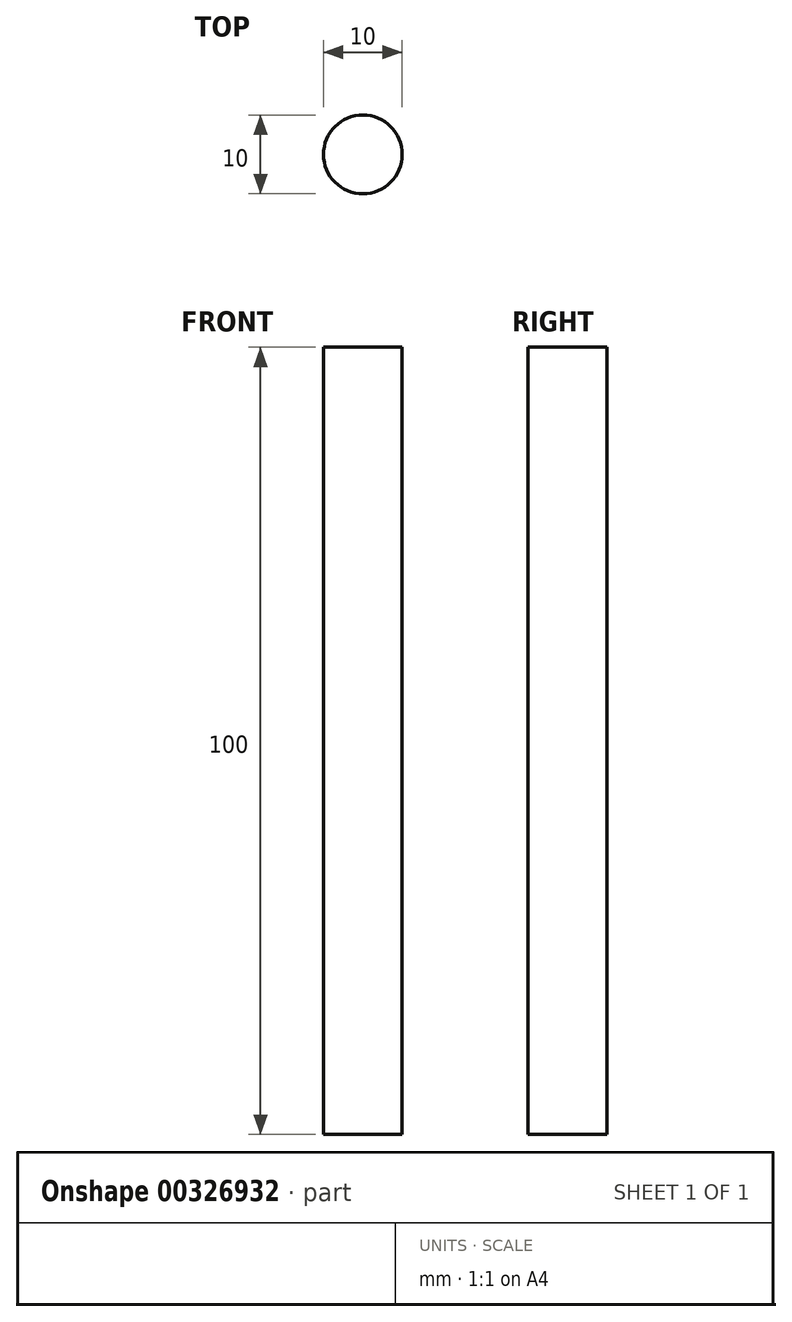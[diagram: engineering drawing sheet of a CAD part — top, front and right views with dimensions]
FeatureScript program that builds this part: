
annotation { "Feature Type Name" : "Feature", "Feature Type Description" : "" }
export const myFeature = defineFeature(function(context is Context, id is Id, definition is map)
    precondition{}
    {
        {
            var Q0;
            Q0=qCreatedBy(makeId("Top.planeOp"),FACE);
            var sketch = newSketch(context, id + "F0", { "sketchPlane" : qUnion([Q0])});
            skCircle(sketch, "E0", {"center": v(0, 0) * mm, "radius": 5 * mm});
            skSolve(sketch);
        }
        {
            var Q0;
            Q0 = qSketchRegion(id + "F0", true);
            extrude(context, id + "F1", {"entities" : qUnion([Q0]), "depth" : 100 * mm});
        }
    });
